# Revit family: CR3B001 Vitocrossal 300 zerlegbar 720kW
name_source: partatom
category: Equipos mecánicos
revit_build: Autodesk Revit 2017 (Build: 20160225_1515(x64)
units: mm (PartAtom-declared; Revit-internal decimal feet)

## family parameters
Compartido = No
Corte con vacíos al cargar = No
Cota de conector redondo = Diámetro de uso
Número OmniClass = 23.75.00.00
Punto de cálculo de habitación = No
Se basa en plano de trabajo = No
Siempre vertical = Sí
Tipo de pieza = Normal
Título OmniClass = Climate Control (HVAC)

## types (1)
- Standard
    Descripción = Vitocrossal 300 zerlegbar 720kW

VIESSMANN Vitocrossal 300, Typ CR3B
Gas-Brennwertkessel.

Nach EN 303 und EN 677, mit
CE-Kennzeichnung. Für geschlossene
Heizungsanlagen mit zul.
Vorlauftemperatur
(=Absicherungstemperatur) bis 110 Grad
C. Für den besonders energiesparenden
Betrieb mit gleitend abgesenkter
Kesselwassertemperatur mit
Brennwertnutzung. Für die Verbrennung
von Gas nach DVGW- Arbeitsblatt G 260.
Brennwertkessel bestehend aus separat
gelieferten Brennkammer- und
Wärmetauscher-Modul. Brennkammer-Modul
mit Edelstahl-Brennraum als
Durchgangsbrennraum mit niedriger
Brennraumbelastung, dadurch
schadstoffarme Verbrennung mit niedrigen
Stickoxid-Emissionen.
Wärmetauscher-Modul mit
Inox-Crossal-Heizflächen aus Edelstahl,
für hochwirksame Brennwertnutzung und
hohe Betriebssicherheit. Alle
Wärmeübertragungsflächen aus Edelstahl
1.4571. Brennwertoptimierte Ausführung
durch spezielle Wasserführung.
Heizkessel mit großem Wasserinhalt, mit
zwei Rücklaufstutzen zum Anschluss von
Heizkreisen mit unterschiedlichen
Temperaturen zur Steigerung des
Brennwertnutzens. Verstärkter
Selbstreinigungseffekt durch die
senkrecht angeordneten, glatten
Edelstahloberflächen, das Kondenswasser
fließt nach unten ab. Kesselkörper
allseitig wärmegedämmt durch 100 mm
starke Verbundwärmedämmung. Leichte und
zeitsparende Montage der
Kesselverkleidung mit VIESSMANN
Fastfix-Montagesystem.

Mit Kesselkreisregelung Vitotronic 100,
Typ GC1B für den Betrieb mit angehobener
Kesselwassertemperatur oder
witterungsgeführten Betrieb in
Verbindung mit einer externen Regelung.
Für den Betrieb mit zweistufigen oder
modulierenden Brennern.
Kesselschutzfunktionen Therm-Control,
Beimischpumpe oder stetige
Rücklauftemperaturregelung (alternativ
zum Speicherladesystem mit geregeltem
3-Wege-Ventil) sind möglich (jeweils
nach Kessel und Anlagenausführung).
Einfache Inbetriebnahme durch Plug and
Work-Funktion. Mit adaptiver
Speichertemperaturregelung (alternativ
Regelung eines Speicherladesystems mit
geregeltem 3-Wege-Ventil), integriertem
Diagnosesystem, Sommersparschaltung und
Pumpenblockierschutz. Mit
Kesseltemperatursensor. Externe Geräte
werden über Rast 5-Systemstecker
angeschlossen. Die Vitotronic 100
enthält: Anlagenschalter,
Schornsteinfeger-Prüfschalter,
TÜV-Taste, elektronischen
Maximaltemperaturbegrenzer,
Temperaturregler und
Sicherheitstemperaturbegrenzer
entsprechend EN 12828, Betriebs- und
Störanzeige, Optolink
Laptop-Schnittstelle und Bedienteil.
Einfache Bedienung mittels grafischem
Display mit Piktogrammen und
kontrastreicher
schwarz/weiß-Darstellung. Möglichkeiten
zur Einstellung von Betriebsprogramm und
Sollwerten sowie zur Abfrage von
Temperaturen. Mit Anschlussmöglichkeit
für externes Anfordern, Kesselfreigabe
und Einschalten der Brennerstufen.
Kommunikationsfähig über KM-BUS und
LON-BUS (durch Einbau des
Kommunikationsmodul LON, Zubehör). Über
KM-BUS ist eine einfache Fernüberwachung
möglich (Vitocom 100 als Zubehör
erforderlich). Über LON-BUS ist die
Fernüberwachung und -bedienung der
Heizungsanlage mit Vitocom 200 (Zubehör)
und Vitodata 100 (Zubehör) möglich. In
Verbindung mit Vitocom 300 (Zubehör) und
Vitodata 300 (Zubehör) ist zusätzlich
die Fernparametrierung möglich. Zugriff
auf Vitodata über PC mit Webbrowser und
Internet. Über LON-BUS und/oder Vitogate
200, Typ EIB
(Zubehör)kommunikationsfähig mit
übergeordneten Leitsystemen.
Datenaustausch mit bis zu 32 Heizkreis-
regelungen Vitotronic 200-H über LON-
BUS ist möglich. Für die Vorgabe des
Kesselwasser- temperatur-Sollwerts über
0-10 V-Eingang, externes Sperren mit
Sammelstörmeldung, Störungsmeldungen und
Ansteuerung Zubringerpumpe zu einer
Unterstation ist eine
Funktionserweiterung der Regelung mit
der Erweiterung EA1 (Zubehör)
erforderlich. Anschluss zusätzlicher
externer Sicherheitseinrichtungen (z.B.
Wassermangelsicherung, Druckbegrenzer
etc.) ist über einen Steckadapter für
externe Sicherheitseinrichtungen
(Zubehör) möglich.

Lieferumfang:
Heizkessel mit Kesseltür (Brennkammer-
und Wärmetauscher-Modul werden separat
ausgeliefert), Abgasdeckel aus
Kunststoff, Abgasssammelkasten,
Gegenflansche mit Schrauben und
Dichtungen, Wärmedämmung,
Brennkammerschauglas, Brennerplatte,
Geruchsverschluss (Siphon) und
Kesselkreisregelung.

Nenn-Wärmeleistung bei:
- Heizbetrieb 50/30 Grad C:      787 kW
- Heizbetrieb 80/60 Grad C:      720 kW
Abmessungen:
- Länge:                       3.021 mm
- Breite:                      1.281 mm
- Höhe:                        1.676 mm
- Gewicht:                     1.553 kg
Einbringmaße-Brennkammermodul:
- Länge:                        1938 mm
- Breite:                        960 mm
- Höhe:                         1676 mm
- Gewicht:                       780 kg
Einbringmaße-Wärmetauschermodul:
- Länge:                        1198 mm
- Breite:                        960 mm
- Höhe:                         1676 mm
- Gewicht:                       615 kg
Inhalt Kesselwasser:            1407 l
Zul. Betriebsdruck:                6 bar
Abgasanschluss:                  300 mm
Norm-Nutzungsgrad:
                bis 98%(Hs)/109%(Hi)

Bestell-Nr.: CR3B001
    Fabricante = Viessmann
    Modelo = CR3B001

## geometry (parser evidence)
native form markers: Sweep x3
no freeform markers — native parametric forms only
